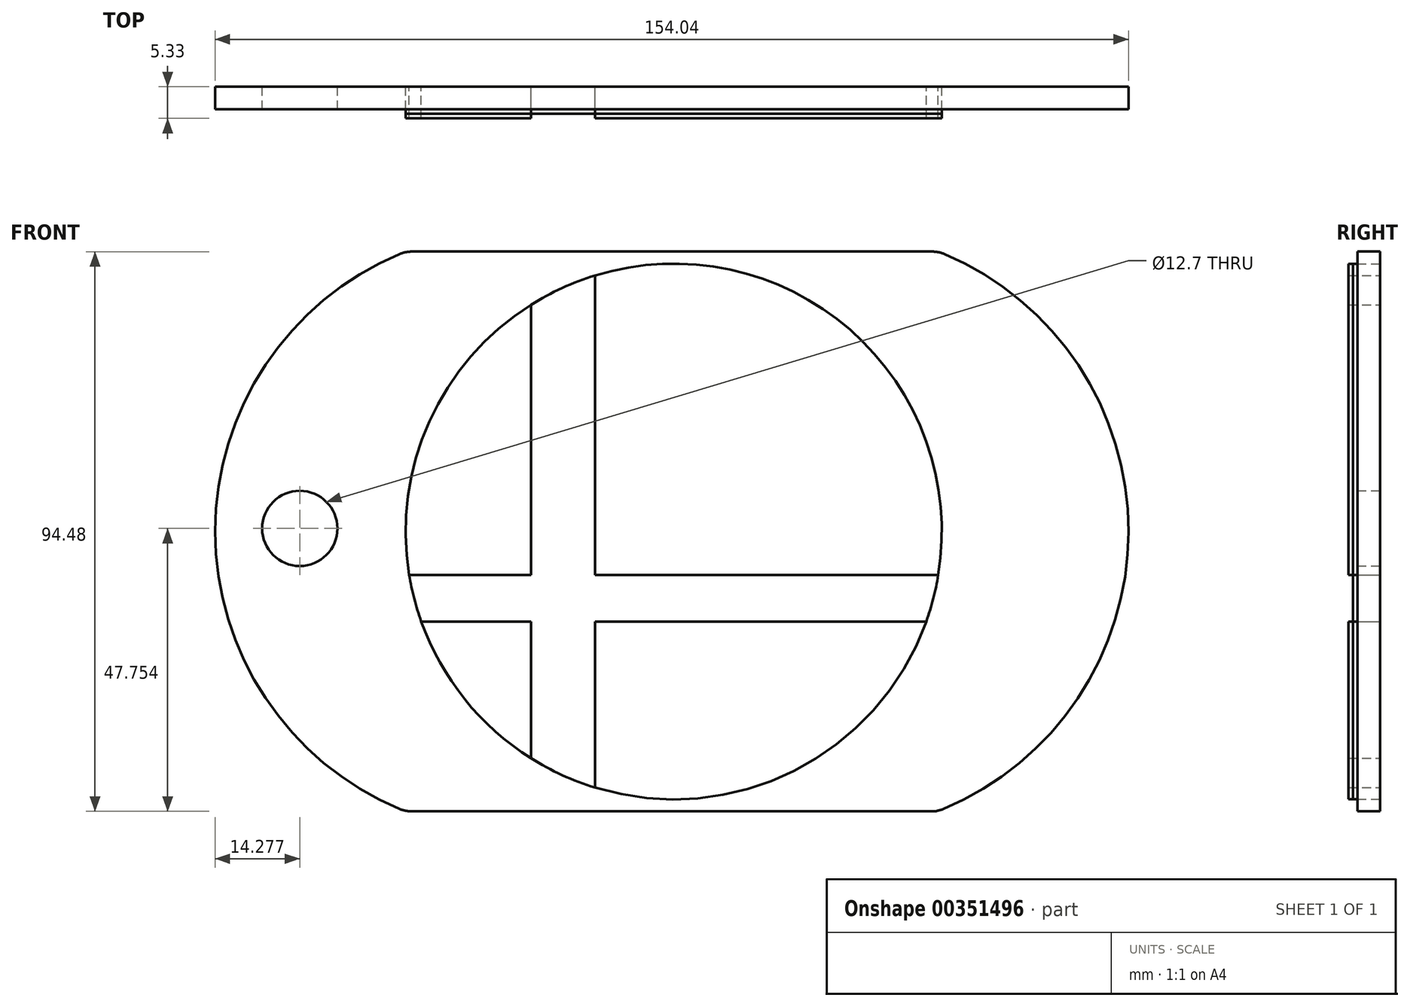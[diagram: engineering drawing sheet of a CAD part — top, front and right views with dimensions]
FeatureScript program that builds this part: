
annotation { "Feature Type Name" : "Feature", "Feature Type Description" : "" }
export const myFeature = defineFeature(function(context is Context, id is Id, definition is map)
    precondition{}
    {
        {
            var Q0;
            Q0=qCreatedBy(makeId("Front.planeOp"),FACE);
            var sketch = newSketch(context, id + "F0", { "sketchPlane" : qUnion([Q0])});
            skCircle(sketch, "E0", {"center": v(0, 0) * mm, "radius": 45.2 * mm});
            skLineSegment(sketch, "E1", {"start": v(-24.07, 38.27) * mm, "end": v(-24.07, -7.36) * mm});
            skLineSegment(sketch, "E2", {"start": v(-44.6, -7.36) * mm, "end": v(-24.07, -7.36) * mm});
            skLineSegment(sketch, "E3", {"start": v(-13.25, 43.22) * mm, "end": v(-13.25, -7.36) * mm});
            skLineSegment(sketch, "E4.trimOffspring", {"start": v(-13.25, -7.36) * mm, "end": v(44.6, -7.36) * mm});
            skLineSegment(sketch, "E5.trimOffspring", {"start": v(-24.07, -15.18) * mm, "end": v(-24.07, -38.27) * mm});
            skLineSegment(sketch, "E6.trimOffspring", {"start": v(-13.25, -15.18) * mm, "end": v(-13.25, -43.22) * mm});
            skLineSegment(sketch, "E7", {"start": v(-42.58, -15.18) * mm, "end": v(-24.07, -15.18) * mm});
            skLineSegment(sketch, "E8", {"start": v(-13.25, -15.18) * mm, "end": v(42.58, -15.18) * mm});
            skSolve(sketch);
        }
        {
            var Q0;
            {var subQ0=sQuery(id+"F0.wireOp",EDGE,"E5.trimOffspring");Q0=makeQuery(id+"F0.imprint","IMPRINT",FACE,{"disambiguationData":[TD([[makeQuery(id+"F0.imprint","IMPRINT",EDGE,{"derivedFrom":subQ0}),-1.0]])]});}
            var Q1;
            {var subQ0=sQuery(id+"F0.wireOp",EDGE,"E6.trimOffspring");Q1=makeQuery(id+"F0.imprint","IMPRINT",FACE,{"disambiguationData":[TD([[makeQuery(id+"F0.imprint","IMPRINT",EDGE,{"derivedFrom":subQ0}),1.0]])]});}
            var Q2;
            {var subQ0=sQuery(id+"F0.wireOp",EDGE,"E3");Q2=makeQuery(id+"F0.imprint","IMPRINT",FACE,{"disambiguationData":[TD([[makeQuery(id+"F0.imprint","IMPRINT",EDGE,{"derivedFrom":subQ0}),1.0]])]});}
            var Q3;
            {var subQ0=sQuery(id+"F0.wireOp",EDGE,"E1");Q3=makeQuery(id+"F0.imprint","IMPRINT",FACE,{"disambiguationData":[TD([[makeQuery(id+"F0.imprint","IMPRINT",EDGE,{"derivedFrom":subQ0}),-1.0]])]});}
            extrude(context, id + "F1", {"entities" : qUnion([Q0, Q1, Q2, Q3]), "depth" : 5.33 * mm});
        }
        {
            var Q0;
            Q0=qCreatedBy(makeId("Front.planeOp"),FACE);
            var sketch = newSketch(context, id + "F2", { "sketchPlane" : qUnion([Q0])});
            skLineSegment(sketch, "E9.bottom", {"start": v(-45.22, 47.24) * mm, "end": v(44.66, 47.24) * mm});
            skLineSegment(sketch, "E9.top", {"start": v(-45.22, -47.24) * mm, "end": v(44.47, -47.24) * mm});
            skArc(sketch, "E10", {"start": v(-45.22, 47.24) * mm, "mid": v(-77.35, 0) * mm, "end": v(-45.22, -47.24) * mm});
            skArc(sketch, "E11", {"start": v(44.47, -47.24) * mm, "mid": v(76.7, -0.06) * mm, "end": v(44.66, 47.24) * mm});
            skCircle(sketch, "E12", {"center": v(-63.07, 0.51) * mm, "radius": 6.35 * mm});
            skSolve(sketch);
        }
        {
            var Q0;
            Q0 = qSketchRegion(id + "F0", true);
            extrude(context, id + "F3", {"entities" : qUnion([Q0]), "depth" : 4.57 * mm});
        }
        {
            var Q0;
            Q0=makeQuery(id+"F2.imprint","IMPRINT",FACE,{"disambiguationData":[TD([[makeQuery(id+"F2.imprint","IMPRINT",EDGE,{"derivedFrom":sQuery(id+"F2.wireOp",EDGE,"E9.bottom")}),-1.0]])]});
            extrude(context, id + "F4", {"entities" : qUnion([Q0]), "depth" : 3.8 * mm});
        }
        {
            var Q0;
            Q0=makeQuery(id+"F4.opExtrude","SWEPT_EDGE",EDGE,{"disambiguationData":[OSD([sQuery(id+"F2.wireOp",EDGE,"E9.bottom"),sQuery(id+"F2.wireOp",EDGE,"E10")])]});
            var Q1;
            Q1=makeQuery(id+"F4.opExtrude","SWEPT_EDGE",EDGE,{"disambiguationData":[OSD([sQuery(id+"F2.wireOp",EDGE,"E9.top"),sQuery(id+"F2.wireOp",EDGE,"E10")])]});
            var Q2;
            Q2=makeQuery(id+"F4.opExtrude","SWEPT_EDGE",EDGE,{"disambiguationData":[OSD([sQuery(id+"F2.wireOp",EDGE,"E9.top"),sQuery(id+"F2.wireOp",EDGE,"E11")])]});
            var Q3;
            Q3=makeQuery(id+"F4.opExtrude","SWEPT_EDGE",EDGE,{"disambiguationData":[OSD([sQuery(id+"F2.wireOp",EDGE,"E9.bottom"),sQuery(id+"F2.wireOp",EDGE,"E11")])]});
            fillet(context, id + "F5", {"entities" : qUnion([Q0, Q1, Q2, Q3]), "radius" : 5.08 * mm, "tangentPropagation" : true, "allowEdgeOverflow" : false});
        }
    });
